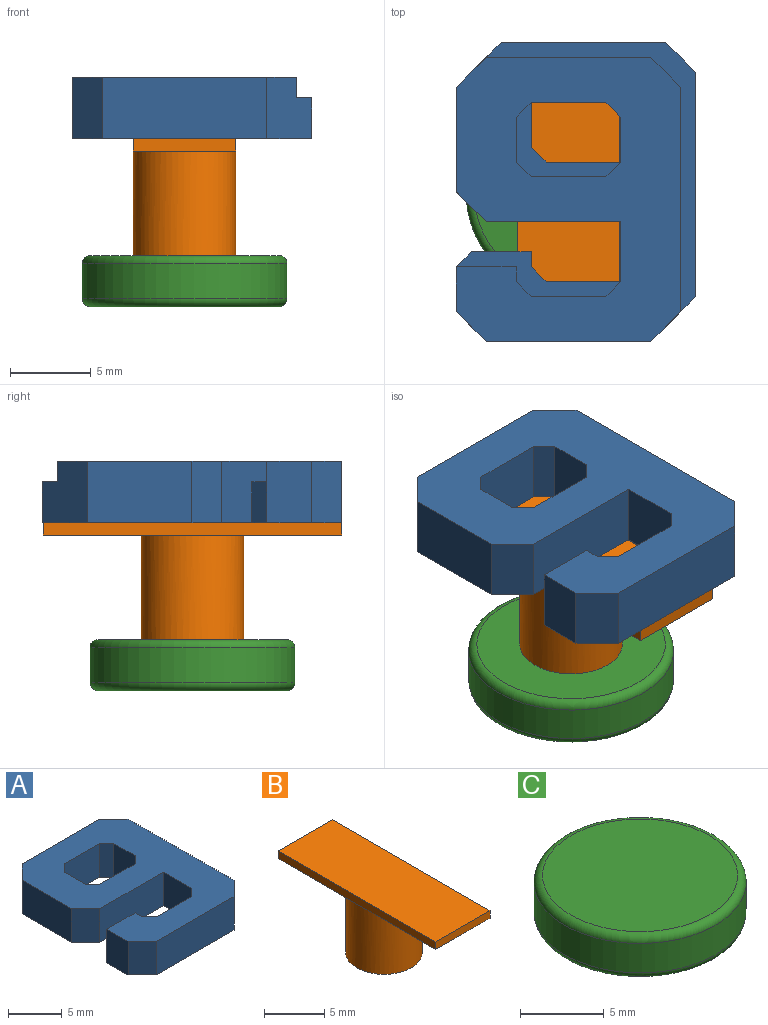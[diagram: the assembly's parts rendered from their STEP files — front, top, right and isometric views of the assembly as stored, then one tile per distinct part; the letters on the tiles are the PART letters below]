
ASSEMBLY  parts=3 mates=2
PART A: 41 faces, bbox 14.8x18.5x3.8 mm
  f0: plane 1.27x0.93mm, normal (0.71,-0.71,0), area 1.7mm2, adj f1,f24,f25,f40
  f1: plane 4.63x3.81mm, normal (0,-1,0), area 17.7mm2, adj f0,f2,f25,f26,f39
  f2: plane 3.81x0.93mm, normal (-0.71,-0.71,0), area 5mm2, adj f1,f3,f25,f26
  f3: plane 3.81x2.78mm, normal (-1,0,0), area 10.6mm2, adj f2,f4,f25,f26,f37
  f4: plane 1.27x0.93mm, normal (-0.71,0.71,0), area 1.7mm2, adj f3,f5,f25,f40
  f5: plane 4.63x1.27mm, normal (0,1,0), area 5.9mm2, adj f4,f6,f25,f40
  f6: plane 1.27x0.93mm, normal (0.71,0.71,0), area 1.7mm2, adj f5,f24,f25,f40
  f7: plane 10.19x1.27mm, normal (0,1,0), area 12.9mm2, adj f8,f23,f25,f30
  f8: plane 3.81x2.78mm, normal (-0.71,0.71,0), area 13.3mm2, adj f7,f9,f25,f26,f29,f30
  f9: plane 6.49x3.81mm, normal (-1,0,0), area 24.7mm2, adj f8,f10,f25,f26
  f10: plane 3.81x1.85mm, normal (-0.71,-0.71,0), area 10mm2, adj f9,f11,f25,f26
  f11: plane 8.34x3.81mm, normal (0,-1,0), area 31.8mm2, adj f10,f12,f25,f26
  f12: plane 3.81x3.71mm, normal (-1,0,0), area 14.1mm2, adj f11,f13,f25,f26,f32
  f13: plane 1.27x0.93mm, normal (-0.71,0.71,0), area 1.7mm2, adj f12,f14,f25,f36
  f14: plane 4.63x1.27mm, normal (0,1,0), area 5.9mm2, adj f13,f15,f25,f36
  f15: plane 1.27x0.93mm, normal (0.71,0.71,0), area 1.7mm2, adj f14,f16,f25,f36
  f16: plane 1.27x0.93mm, normal (1,0,0), area 1.2mm2, adj f15,f17,f25,f36
  f17: plane 3.71x1.27mm, normal (0,1,0), area 4.7mm2, adj f16,f18,f25,f36
  f18: plane 3.81x2.78mm, normal (-1,0,0), area 10.6mm2, adj f17,f19,f25,f26,f31
  f19: plane 3.81x1.85mm, normal (-0.71,-0.71,0), area 10mm2, adj f18,f20,f25,f26
  f20: plane 10.19x3.81mm, normal (0,-1,0), area 38.8mm2, adj f19,f21,f25,f26
  f21: plane 3.81x2.78mm, normal (0.71,-0.71,0), area 13.3mm2, adj f20,f22,f25,f26,f27,f30
  f22: plane 13.9x1.27mm, normal (1,0,0), area 17.7mm2, adj f21,f23,f25,f30
  f23: plane 1.85x1.85mm, normal (0.71,0.71,0), area 3.3mm2, adj f7,f22,f25,f30
  f24: plane 2.78x1.27mm, normal (1,0,0), area 3.5mm2, adj f0,f6,f25,f40
  f25: plane 17.61x13.9mm, normal (0,0,1), area 168.3mm2, adj f0,f1,f2,f3,f4,f5,f6,f7
  f26: plane 18.53x14.83mm, normal (0,0,-1), area 213mm2, adj f1,f2,f3,f8,f9,f10,f11,f12
  f27: plane 13.9x2.54mm, normal (1,0,0), area 35.3mm2, adj f21,f26,f28,f30
  f28: plane 2.54x1.85mm, normal (0.71,0.71,0), area 6.7mm2, adj f26,f27,f29,f30
  f29: plane 10.19x2.54mm, normal (0,1,0), area 25.9mm2, adj f8,f26,f28,f30
  f30: plane 16.68x12.97mm, normal (0,0,1), area 25.8mm2, adj f7,f8,f21,f22,f23,f27,f28,f29
  f31: plane 2.54x0.93mm, normal (-0.71,0.71,0), area 3.3mm2, adj f18,f26,f35,f36
  f32: plane 4.63x2.54mm, normal (0,1,0), area 11.8mm2, adj f12,f26,f33,f36
  f33: plane 2.54x0.93mm, normal (0.71,0.71,0), area 3.3mm2, adj f26,f32,f34,f36
  f34: plane 2.54x0.93mm, normal (1,0,0), area 2.4mm2, adj f26,f33,f35,f36
  f35: plane 3.71x2.54mm, normal (0,1,0), area 9.4mm2, adj f26,f31,f34,f36
  f36: plane 10.19x2.78mm, normal (0,0,1), area 10.3mm2, adj f13,f14,f15,f16,f17,f31,f32,f33
  f37: plane 4.63x2.54mm, normal (0,1,0), area 11.8mm2, adj f3,f26,f38,f40
  f38: plane 2.54x0.93mm, normal (0.71,0.71,0), area 3.3mm2, adj f26,f37,f39,f40
  f39: plane 2.78x2.54mm, normal (1,0,0), area 7.1mm2, adj f1,f26,f38,f40
  f40: plane 6.49x4.63mm, normal (0,0,1), area 8.6mm2, adj f0,f4,f5,f6,f24,f37,f38,f39
PART B: 9 faces, bbox 6.4x18.5x7.2 mm
  f0: cylinder r=3.17mm len=6.48mm, axis (0,0,-1), area 129.2mm2, adj f1,f2,f8
  f1: plane 6.35x6.35mm, normal (0,0,-1), area 31.7mm2, adj f0
  f2: plane 9.24x6.35mm, normal (0,0,-1), area 42.8mm2, adj f0,f4,f5,f6
  f3: plane 6.35x0.76mm, normal (0,-1,0), area 4.8mm2, adj f4,f6,f7,f8
  f4: plane 18.48x0.76mm, normal (1,0,0), area 14.1mm2, adj f2,f3,f5,f7,f8
  f5: plane 6.35x0.76mm, normal (0,1,0), area 4.8mm2, adj f2,f4,f6,f7
  f6: plane 18.48x0.76mm, normal (-1,0,0), area 14.1mm2, adj f2,f3,f5,f7,f8
  f7: plane 18.48x6.35mm, normal (0,0,1), area 117.3mm2, adj f3,f4,f5,f6
  f8: plane 9.24x6.35mm, normal (0,0,-1), area 42.8mm2, adj f0,f3,f4,f6
PART C: 5 faces, bbox 13.7x13.7x3.2 mm
  f0: cylinder r=6.35mm len=12.7mm, axis (0,0,1), area 86.1mm2, adj f3,f4
  f1: plane 11.68x11.68mm, normal (0,0,-1), area 107.2mm2, adj f4
  f2: plane 11.68x11.68mm, normal (0,0,1), area 107.2mm2, adj f3
  f3: torus R=5.84mm, axis (0,0,1), area 30.9mm2, adj f0,f2
  f4: torus R=5.84mm, axis (0,0,1), area 30.9mm2, adj f0,f1
PLACE A t=(-7.28,-6.38,5.19)mm
PLACE B t=(-0.33,2.86,-2.05)mm
PLACE C t=(-0.33,2.86,-2.05)mm
MATE planar A.f20 <-> B.f3  axis (0,-1,0) through (-0.33,-6.38,7.09)mm
MATE planar A.f26 <-> B.f0  axis (0,0,-1) through (0.4,3.02,5.19)mm
